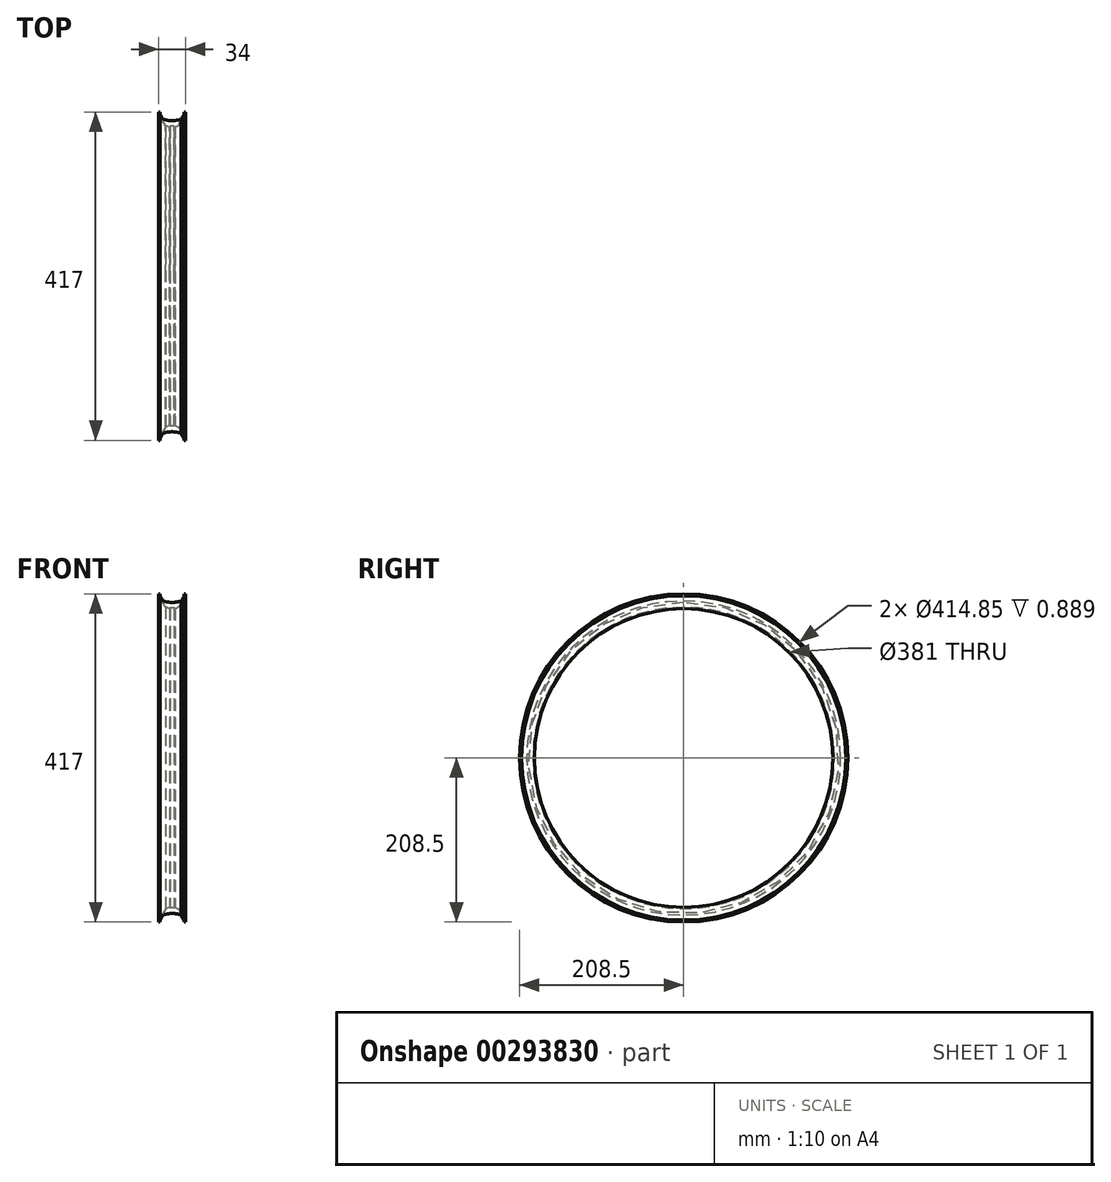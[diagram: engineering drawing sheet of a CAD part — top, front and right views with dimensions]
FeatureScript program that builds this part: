
annotation { "Feature Type Name" : "Feature", "Feature Type Description" : "" }
export const myFeature = defineFeature(function(context is Context, id is Id, definition is map)
    precondition{}
    {
        {
            var Q0;
            Q0=qCreatedBy(makeId("Front.planeOp"),FACE);
            var sketch = newSketch(context, id + "F0", { "sketchPlane" : qUnion([Q0])});
            skLineSegment(sketch, "E0", {"start": v(0, 0) * mm, "end": v(0, 190.5) * mm, "construction": true});
            skLineSegment(sketch, "E1", {"start": v(8.36, 0) * mm, "end": v(129.82, 0) * mm, "construction": true});
            skLineSegment(sketch, "E2", {"start": v(8.17, 191.45) * mm, "end": v(17, 205.96) * mm});
            skLineSegment(sketch, "E3", {"start": v(17, 205.96) * mm, "end": v(17, 208.5) * mm});
            skLineSegment(sketch, "E4", {"start": v(17, 208.5) * mm, "end": v(15.22, 208.5) * mm});
            skLineSegment(sketch, "E5", {"start": v(15.22, 208.5) * mm, "end": v(15.22, 207.42) * mm});
            skLineSegment(sketch, "E6", {"start": v(15.22, 207.42) * mm, "end": v(16.11, 207.42) * mm});
            skLineSegment(sketch, "E7", {"start": v(16.11, 207.42) * mm, "end": v(16.11, 206.94) * mm});
            skLineSegment(sketch, "E8", {"start": v(16.11, 206.94) * mm, "end": v(11.57, 199.48) * mm});
            skArc(sketch, "E9", {"start": v(0, 197.61) * mm, "mid": v(5.86, 198.08) * mm, "end": v(11.57, 199.48) * mm});
            skLineSegment(sketch, "E10", {"start": v(0, 197.61) * mm, "end": v(-22.7, 197.61) * mm, "construction": true});
            skLineSegment(sketch, "E11", {"start": v(0, 190.5) * mm, "end": v(0, 197.61) * mm, "construction": true});
            skLineSegment(sketch, "E12", {"start": v(3.44, 189.6) * mm, "end": v(8.17, 191.45) * mm});
            skLineSegment(sketch, "E13", {"start": v(2.54, 190.5) * mm, "end": v(3.44, 189.6) * mm});
            skLineSegment(sketch, "E14", {"start": v(2.54, 190.5) * mm, "end": v(0, 190.5) * mm});
            skLineSegment(sketch, "E15.MirrorCS", {"start": v(-16.11, 207.42) * mm, "end": v(-16.11, 206.94) * mm});
            skLineSegment(sketch, "E16.MirrorCS", {"start": v(-2.54, 190.5) * mm, "end": v(-3.44, 189.6) * mm});
            skLineSegment(sketch, "E17.MirrorCS", {"start": v(-15.22, 207.42) * mm, "end": v(-16.11, 207.42) * mm});
            skLineSegment(sketch, "E18.MirrorCS", {"start": v(-17, 208.5) * mm, "end": v(-15.22, 208.5) * mm});
            skLineSegment(sketch, "E19.MirrorCS", {"start": v(-15.22, 208.5) * mm, "end": v(-15.22, 207.42) * mm});
            skArc(sketch, "E20.MirrorCS", {"start": v(0, 197.61) * mm, "mid": v(-5.86, 198.08) * mm, "end": v(-11.57, 199.48) * mm});
            skLineSegment(sketch, "E21.MirrorCS", {"start": v(-16.11, 206.94) * mm, "end": v(-11.57, 199.48) * mm});
            skLineSegment(sketch, "E22.MirrorCS", {"start": v(-3.44, 189.6) * mm, "end": v(-8.17, 191.45) * mm});
            skLineSegment(sketch, "E23.MirrorCS", {"start": v(-17, 205.96) * mm, "end": v(-17, 208.5) * mm});
            skLineSegment(sketch, "E24.MirrorCS", {"start": v(-8.17, 191.45) * mm, "end": v(-17, 205.96) * mm});
            skLineSegment(sketch, "E25.MirrorCS", {"start": v(-2.54, 190.5) * mm, "end": v(0, 190.5) * mm});
            skPoint(sketch, "E26", {"position": v(-16.11, 208.5) * mm});
            skSolve(sketch);
        }
        {
            var Q0;
            Q0=makeQuery(id+"F0.imprint","IMPRINT",FACE,{"disambiguationData":[TD([[makeQuery(id+"F0.imprint","IMPRINT",EDGE,{"derivedFrom":sQuery(id+"F0.wireOp",EDGE,"E2")}),1.0]])]});
            var Q1;
            Q1=sQuery(id+"F0.wireOp",EDGE,"E1");
            revolve(context, id + "F1", {"entities" : qUnion([Q0]), "axis" : qUnion([Q1]), "revolveType" : RevolveType.FULL});
        }
        {
            var Q0;
            Q0=makeQuery(id+"F1.opRevolve","SWEPT_EDGE",EDGE,{"disambiguationData":[OSD([sQuery(id+"F0.wireOp",EDGE,"E20.MirrorCS"),sQuery(id+"F0.wireOp",EDGE,"E21.MirrorCS")])]});
            var Q1;
            Q1=makeQuery(id+"F1.opRevolve","SWEPT_EDGE",EDGE,{"disambiguationData":[OSD([sQuery(id+"F0.wireOp",EDGE,"E2"),sQuery(id+"F0.wireOp",EDGE,"E12")])]});
            fillet(context, id + "F2", {"entities" : qUnion([Q0, Q1]), "radius" : 5.08 * mm, "tangentPropagation" : true, "allowEdgeOverflow" : false});
        }
    });
